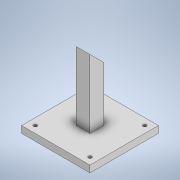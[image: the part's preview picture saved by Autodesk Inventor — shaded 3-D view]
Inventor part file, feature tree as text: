
AUTODESK INVENTOR PART (.ipt)
format: ipt  version: 2022 (Build 260153000, 153)  size: 131,072 bytes
history: native  units: mm
features: extrude x4, sketch x4
ambient origin geometry x8: Origin, YZ Plane, XZ Plane, XY Plane, X Axis, Y Axis, Z Axis, Center Point
bodies: Solid1 (feature_tree)
feature tree (8):
  extrude  "Extrusion1"  Depth=2.0mm
  extrude  "Extrusion2"  TaperAngle=45.0deg  [1 undecoded]
  extrude  "Extrusion3"  Depth=10.0mm
  extrude  "Extrusion4"  Depth=4.0mm
  sketch  "Sketch2"  dims[d5=2.0mm d6=2.0mm]
  sketch  "Sketch3"  dims[d7=10.0mm d8=0.0mm d9=45.0deg]
  sketch  "Sketch4"  dims[d10=0.0mm d11=0.0mm d12=10.0mm]
  sketch  "Sketch5"  dims[d13=10.0mm d14=4.0mm d15=4.0mm d16=1.0mm d17=0.0mm d18=0.5mm d20=9.0mm d22=1.0mm d23=20.0mm d25=8.0mm d26=20.0mm d28=8.0mm d31=0.0mm d32=0.0mm]
note: 1 required parameter value undecoded (feature->parameter linkage not recoverable at this tier; creation-order binding heuristic only, values carry confidence <= 0.55)
